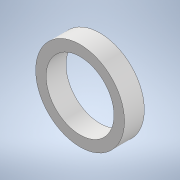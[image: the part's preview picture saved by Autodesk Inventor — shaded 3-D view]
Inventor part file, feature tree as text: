
AUTODESK INVENTOR PART (.ipt)
format: ipt  version: 2022.3 (Build 263350000, 350)  size: 178,176 bytes
history: native  units: mm
features: reference x140, other x5, extrude x4, sketch x4, projected_geometry x2
ambient origin geometry x8: Origin, YZ Plane, XZ Plane, XY Plane, X Axis, Y Axis, Z Axis, Center Point
bodies: Solid1 (feature_tree)
feature tree (155):
  extrude  "Extrusion1"  Depth=2.5mm TaperAngle=0.0deg
  extrude  "Extrusion2"  Depth=2.0mm TaperAngle=0.0deg
  extrude  "Extrusion3"  [1 undecoded]
  extrude  "Extrusion4"  [1 undecoded]
  sketch  "Sketch1"  dims[d0=1.0mm d1=2.5mm d2=0.0mm]
  reference  "Reference1"
  reference  "Reference2"
  reference  "Reference3"
  reference  "Reference4"
  reference  "Reference5"
  reference  "Reference6"
  reference  "Reference7"
  reference  "Reference8"
  reference  "Reference9"
  reference  "Reference10"
  reference  "Reference11"
  reference  "Reference12"
  reference  "Reference13"
  reference  "Reference14"
  reference  "Reference15"
  reference  "Reference16"
  reference  "Reference17"
  reference  "Reference18"
  reference  "Reference19"
  reference  "Reference20"
  reference  "Reference21"
  reference  "Reference22"
  reference  "Reference23"
  reference  "Reference24"
  reference  "Reference25"
  reference  "Reference26"
  reference  "Reference27"
  reference  "Reference28"
  reference  "Reference29"
  reference  "Reference30"
  reference  "Reference31"
  reference  "Reference32"
  reference  "Reference33"
  reference  "Reference34"
  reference  "Reference35"
  reference  "Reference36"
  reference  "Reference37"
  reference  "Reference38"
  reference  "Reference39"
  reference  "Reference40"
  reference  "Reference41"
  reference  "Reference42"
  reference  "Reference43"
  reference  "Reference44"
  reference  "Reference45"
  reference  "Reference46"
  reference  "Reference47"
  reference  "Reference48"
  reference  "Reference49"
  reference  "Reference50"
  reference  "Reference51"
  reference  "Reference52"
  reference  "Reference53"
  reference  "Reference54"
  reference  "Reference55"
  reference  "Reference56"
  reference  "Reference57"
  reference  "Reference58"
  reference  "Reference59"
  reference  "Reference60"
  reference  "Reference61"
  reference  "Reference62"
  reference  "Reference63"
  reference  "Reference64"
  reference  "Reference65"
  reference  "Reference66"
  reference  "Reference67"
  reference  "Reference68"
  reference  "Reference69"
  reference  "Reference70"
  reference  "Reference71"
  reference  "Reference72"
  reference  "Reference73"
  reference  "Reference74"
  reference  "Reference75"
  reference  "Reference76"
  reference  "Reference77"
  reference  "Reference78"
  reference  "Reference79"
  reference  "Reference80"
  reference  "Reference81"
  reference  "Reference82"
  reference  "Reference83"
  reference  "Reference84"
  reference  "Reference85"
  reference  "Reference86"
  reference  "Reference87"
  reference  "Reference88"
  reference  "Reference89"
  reference  "Reference90"
  reference  "Reference91"
  reference  "Reference92"
  reference  "Reference93"
  reference  "Reference94"
  reference  "Reference95"
  reference  "Reference96"
  reference  "Reference97"
  reference  "Reference98"
  reference  "Reference99"
  reference  "Reference100"
  reference  "Reference101"
  reference  "Reference102"
  reference  "Reference103"
  reference  "Reference104"
  reference  "Reference105"
  reference  "Reference106"
  reference  "Reference107"
  reference  "Reference108"
  reference  "Reference109"
  reference  "Reference110"
  reference  "Reference111"
  reference  "Reference112"
  reference  "Reference113"
  reference  "Reference114"
  reference  "Reference115"
  reference  "Reference116"
  reference  "Reference117"
  reference  "Reference118"
  reference  "Reference119"
  reference  "Reference120"
  reference  "Reference121"
  reference  "Reference122"
  reference  "Reference123"
  reference  "Reference124"
  reference  "Reference125"
  reference  "Reference126"
  reference  "Reference127"
  reference  "Reference128"
  reference  "Reference129"
  reference  "Reference130"
  reference  "Reference131"
  reference  "Reference132"
  reference  "Reference133"
  reference  "Reference134"
  reference  "Reference135"
  reference  "Reference136"
  reference  "Reference137"
  reference  "Reference138"
  sketch  "Sketch2"  dims[d3=2.0mm d4=0.0mm d5=2.0mm d6=0.0mm]
  projected_geometry  "Projected Loop1"
  reference  "Reference139"
  sketch  "Sketch3"  dims[d7=0.4mm d8=0.0mm]
  reference  "Reference140"
  sketch  "Sketch4"
  projected_geometry  "Projected Loop2"
  other  "Assembly1"
  other  "Moteur - Engrenage 3:2"
  other  "Moteur - Engrenage 4:1"
  other  "Moteur - Engrenage 4:2"
  other  "Moteur - Engrenage 3:1"
note: 2 required parameter values undecoded (feature->parameter linkage not recoverable at this tier; creation-order binding heuristic only, values carry confidence <= 0.55)
